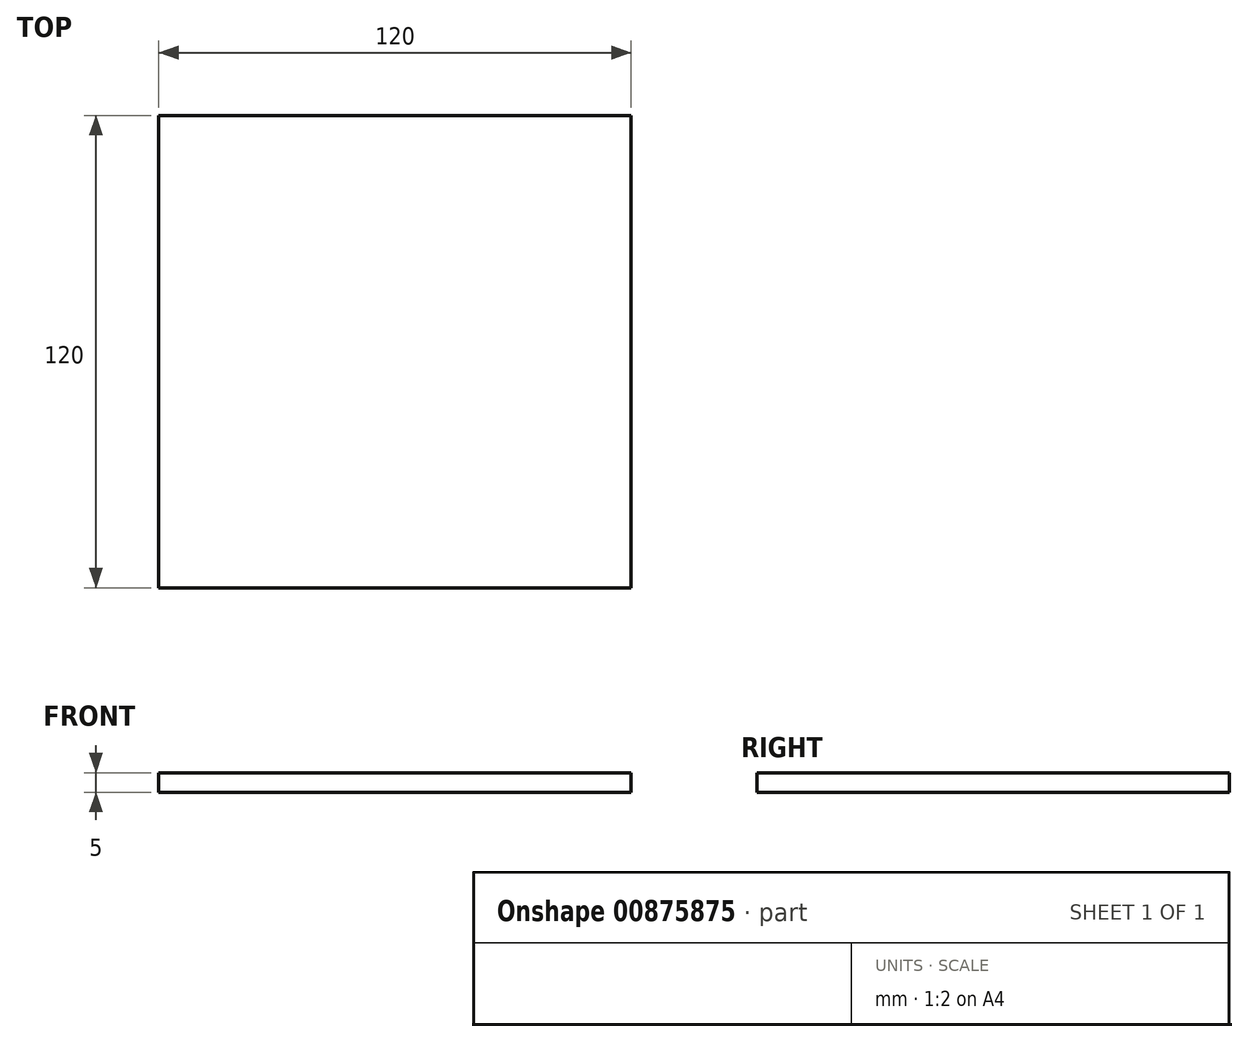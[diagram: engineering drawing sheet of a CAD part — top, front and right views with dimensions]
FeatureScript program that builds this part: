
annotation { "Feature Type Name" : "Feature", "Feature Type Description" : "" }
export const myFeature = defineFeature(function(context is Context, id is Id, definition is map)
    precondition{}
    {
        {
            var Q0;
            Q0=qCreatedBy(makeId("Top.planeOp"),FACE);
            var sketch = newSketch(context, id + "F0", { "sketchPlane" : qUnion([Q0])});
            skLineSegment(sketch, "E0.bottom", {"start": v(60, -60) * mm, "end": v(-60, -60) * mm});
            skLineSegment(sketch, "E0.top", {"start": v(60, 60) * mm, "end": v(-60, 60) * mm});
            skLineSegment(sketch, "E0.left", {"start": v(60, -60) * mm, "end": v(60, 60) * mm});
            skLineSegment(sketch, "E0.right", {"start": v(-60, -60) * mm, "end": v(-60, 60) * mm});
            skPoint(sketch, "E0.middle", {"position": v(0, 0) * mm});
            skSolve(sketch);
        }
        {
            var Q0;
            Q0=makeQuery(id+"F0.imprint","IMPRINT",FACE,{"disambiguationData":[TD([[makeQuery(id+"F0.imprint","IMPRINT",EDGE,{"derivedFrom":sQuery(id+"F0.wireOp",EDGE,"E0.bottom")}),-1.0]])]});
            extrude(context, id + "F1", {"entities" : qUnion([Q0]), "depth" : 5 * mm, "offsetDistance" : 25 * mm});
        }
    });
